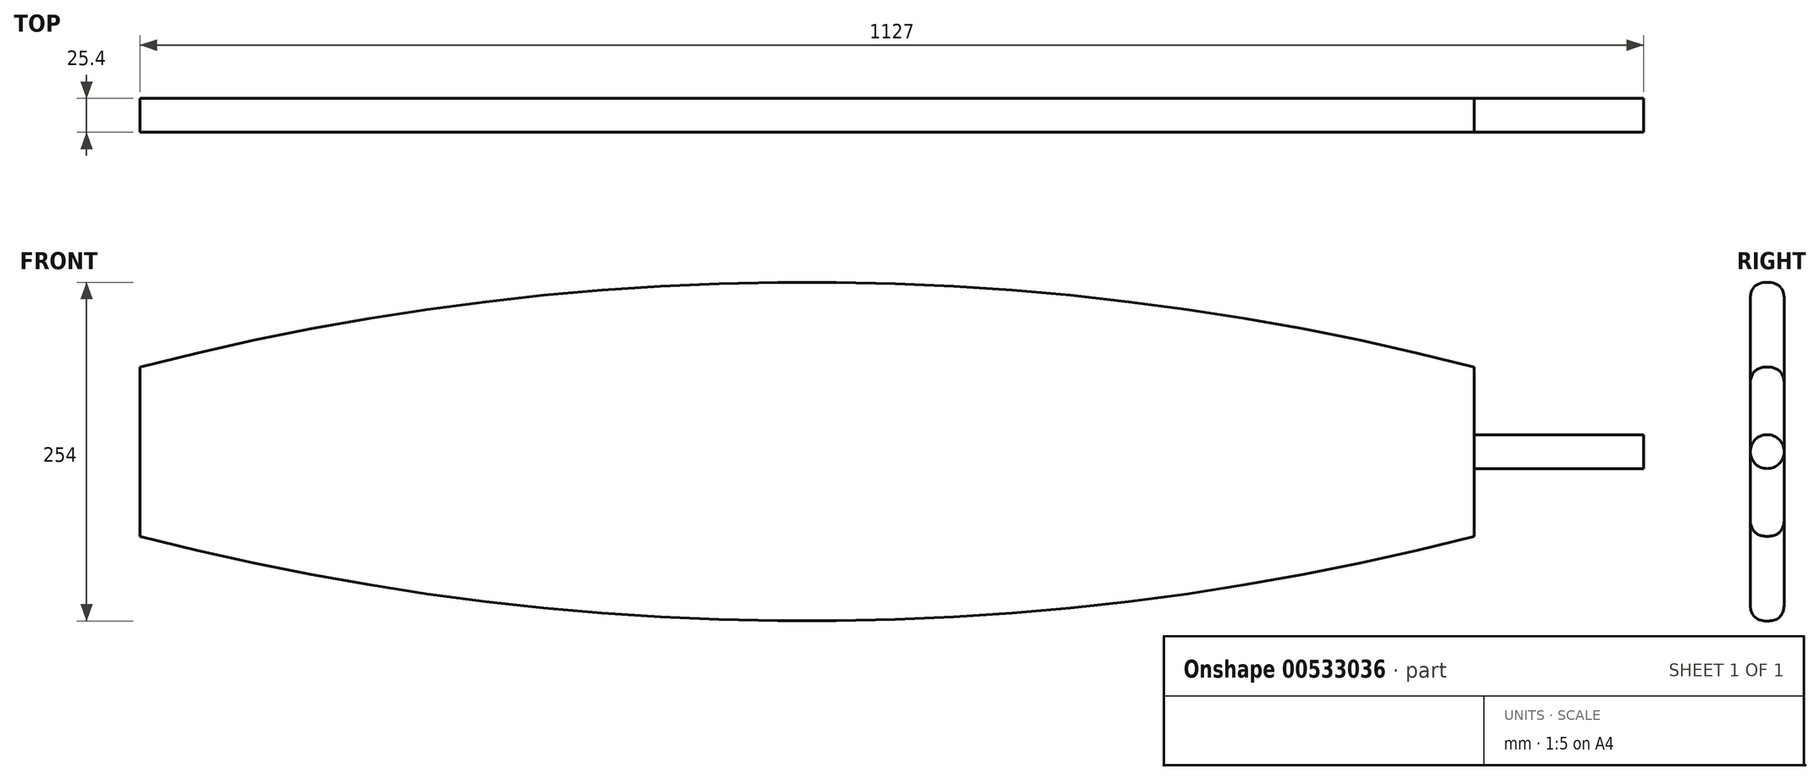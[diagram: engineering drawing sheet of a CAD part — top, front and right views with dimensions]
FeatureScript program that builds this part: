
annotation { "Feature Type Name" : "Feature", "Feature Type Description" : "" }
export const myFeature = defineFeature(function(context is Context, id is Id, definition is map)
    precondition{}
    {
        {
            var Q0;
            Q0=qCreatedBy(makeId("Front.planeOp"),FACE);
            var sketch = newSketch(context, id + "F0", { "sketchPlane" : qUnion([Q0])});
            skLineSegment(sketch, "E0.left", {"start": v(500, -63.5) * mm, "end": v(500, 63.5) * mm});
            skLineSegment(sketch, "E0.right", {"start": v(-500, -63.5) * mm, "end": v(-500, 63.5) * mm});
            skPoint(sketch, "E0.middle", {"position": v(0, 0) * mm});
            skArc(sketch, "E1", {"start": v(500, 63.5) * mm, "mid": v(0, 127) * mm, "end": v(-500, 63.5) * mm});
            skArc(sketch, "E2", {"start": v(-500, -63.5) * mm, "mid": v(0, -127) * mm, "end": v(500, -63.5) * mm});
            skPoint(sketch, "E3.orphan", {"position": v(500, 127) * mm});
            skPoint(sketch, "E4.orphan", {"position": v(-500, 127) * mm});
            skPoint(sketch, "E5.orphan", {"position": v(-500, -127) * mm});
            skPoint(sketch, "E6.orphan", {"position": v(500, -127) * mm});
            skSolve(sketch);
        }
        {
            var Q0;
            Q0 = qSketchRegion(id + "F0", true);
            extrude(context, id + "F1", {"entities" : qUnion([Q0]), "endBound" : BoundingType.SYMMETRIC, "depth" : 25.4 * mm, "offsetDistance" : 25.4 * mm});
        }
        {
            var Q0;
            Q0=makeQuery(id+"F1.opExtrude","SWEPT_FACE",FACE,{"disambiguationData":[OSD([sQuery(id+"F0.wireOp",EDGE,"E0.left")])]});
            var sketch = newSketch(context, id + "F2", { "sketchPlane" : qUnion([Q0])});
            skCircle(sketch, "E7", {"center": v(0, 0) * mm, "radius": 12.7 * mm});
            skSolve(sketch);
        }
        {
            var Q0;
            Q0 = qSketchRegion(id + "F2", true);
            var Q1;
            Q1=makeQuery(id+"F1.opExtrude","SWEPT_FACE",FACE,{"disambiguationData":[OSD([sQuery(id+"F0.wireOp",EDGE,"E0.right")])]});
            extrude(context, id + "F3", {"entities" : qUnion([Q0, Q1]), "operationType" : NewBodyOperationType.ADD, "depth" : 127 * mm, "offsetDistance" : 25.4 * mm});
        }
        {
            var Q0;
            Q0=makeQuery(id+"F1.opExtrude","CAP_EDGE",EDGE,{"disambiguationData":[OSD([sQuery(id+"F0.wireOp",EDGE,"E1")])],"isStart":false});
            var Q1;
            Q1=makeQuery(id+"F1.opExtrude","CAP_EDGE",EDGE,{"disambiguationData":[OSD([sQuery(id+"F0.wireOp",EDGE,"E1")])],"isStart":true});
            fillet(context, id + "F4", {"entities" : qUnion([Q0, Q1]), "tangentPropagation" : true, "crossSection" : FilletCrossSection.CONIC, "radius" : 12.7 * mm, "rho" : 0.5, "defaultsChanged" : false, "vertexSettings" : [], "allowEdgeOverflow" : false});
        }
        {
            var Q0;
            Q0=makeQuery(id+"F1.opExtrude","CAP_EDGE",EDGE,{"disambiguationData":[OSD([sQuery(id+"F0.wireOp",EDGE,"E2")])],"isStart":false});
            var Q1;
            Q1=makeQuery(id+"F1.opExtrude","CAP_EDGE",EDGE,{"disambiguationData":[OSD([sQuery(id+"F0.wireOp",EDGE,"E2")])],"isStart":true});
            fillet(context, id + "F5", {"entities" : qUnion([Q0, Q1]), "tangentPropagation" : true, "crossSection" : FilletCrossSection.CONIC, "radius" : 12.7 * mm, "rho" : 0.5, "defaultsChanged" : true, "vertexSettings" : [], "allowEdgeOverflow" : false});
        }
    });
